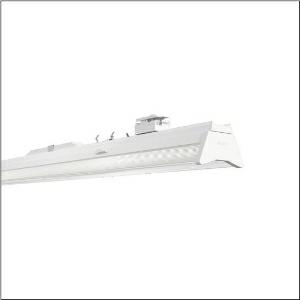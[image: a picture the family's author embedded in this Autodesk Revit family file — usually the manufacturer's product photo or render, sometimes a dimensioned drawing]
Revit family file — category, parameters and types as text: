
# Revit family: licross_r__21_performance_mo_51td16vnd65g_0ec4
name_source: partatom
category: Lighting Fixtures
units: mm (PartAtom-declared; Revit-internal decimal feet)

## family parameters
Cut with Voids When Loaded = No
Host = Face
Light Source = No
Part Type = Normal
Room Calculation Point = No
Round Connector Dimension = Use Diameter
Shared = No

## types (1)
- --- (1 x LED, 6500 lm, 38.7 W, 4000K)
    Apparent Load = 39 VA
    CIE Flux Codes = 66 88 96 79 100
    Color Rendering = 90
    Color Temperature = 4000K
    Default Elevation = 1800 mm
    Description = Licross® 21 Performance MO, luminaire insert, of sheet steel, galvanised, coil coated, white, length: 1.500mm, width: 120mm, height: 123mm, LED rated luminous flux: 6.500lm, light colour: 940, control gear: DALI 2, CLO, with plug, 5-pole, with phase selection, mains connection: 220..240V, AC, 50/60Hz, start of lifetime: 39W, end of service life: 43W, internal wiring halogen-free, primary light control with lens, of plastic, primary optical cover: cover, of PMMA, light emission: direct/indirect distribution, primary light characteristic: symmetric, protection rating (complete): IP54, insulation class (complete): insulation class I (protective earthing), certification: CE, ENEC, VDE, UKCA, protection symbol: D if used in an environment with non-conductive dust loads with corresponding accessories, impact resistance: IK06, permissible ambient temperature for indoor applications: -25..+40°C, corresponds to IFS (International Featured Standards) requirements for safety and quality in the food industry, reducing of maximum allowable ambient temperature of 5°C with ceiling mounting, LABS conformity tested according to VDMA 24364:2018-05, packaging unit: 1 piece
    Height = 114 mm
    Lamp = 1 x LED
    Lamp Light Flux = 6500 lm
    Lamp Power = 38.7 W
    Lamp count = 1
    Length = 1500 mm
    Luminous efficacy = 168 lm/W
    Manufacturer = Siteco
    ModVariant = No
    Model = 51TD16VND65G
    Mounting Place = Ceiling
    Mounting Type = Pendant
    Number of Poles = 1
    OnlyDefault = Yes
    Power Factor = 1
    Product Name = Licross® 21 Performance MO
    Product group = luminaire insert | ceiling pendant
    ProductGroupID = 902
    Protection Class = Protection class I
    Protection Degree = IP 54
    RLX_Detail_Level = 1
    RLX_Emergency_Light_Flux = 0 lm
    RLX_Emergency_Type = 0
    RLX_Emergency_Type_DB = No
    RlxData = <blob elided: 34173 chars, md5=189a11df>
    Socket = socket
    Standby Power = 0 W
    System Light Flux = 6500 lm
    System Power = 39 W
    Type Comments = factory setting: luminous flux: 100 % | dim-lin: 254 | 258 mA
    Type Image = l_1256138.jpg
    URL = http://relux.com
    VarID = @adj_107655
    Voltage = 0 V
    Weight = 0.00 kg
    Width = 120 mm

## geometry (parser evidence)
native form markers: Blend x4, Sweep x13
no freeform markers — native parametric forms only
